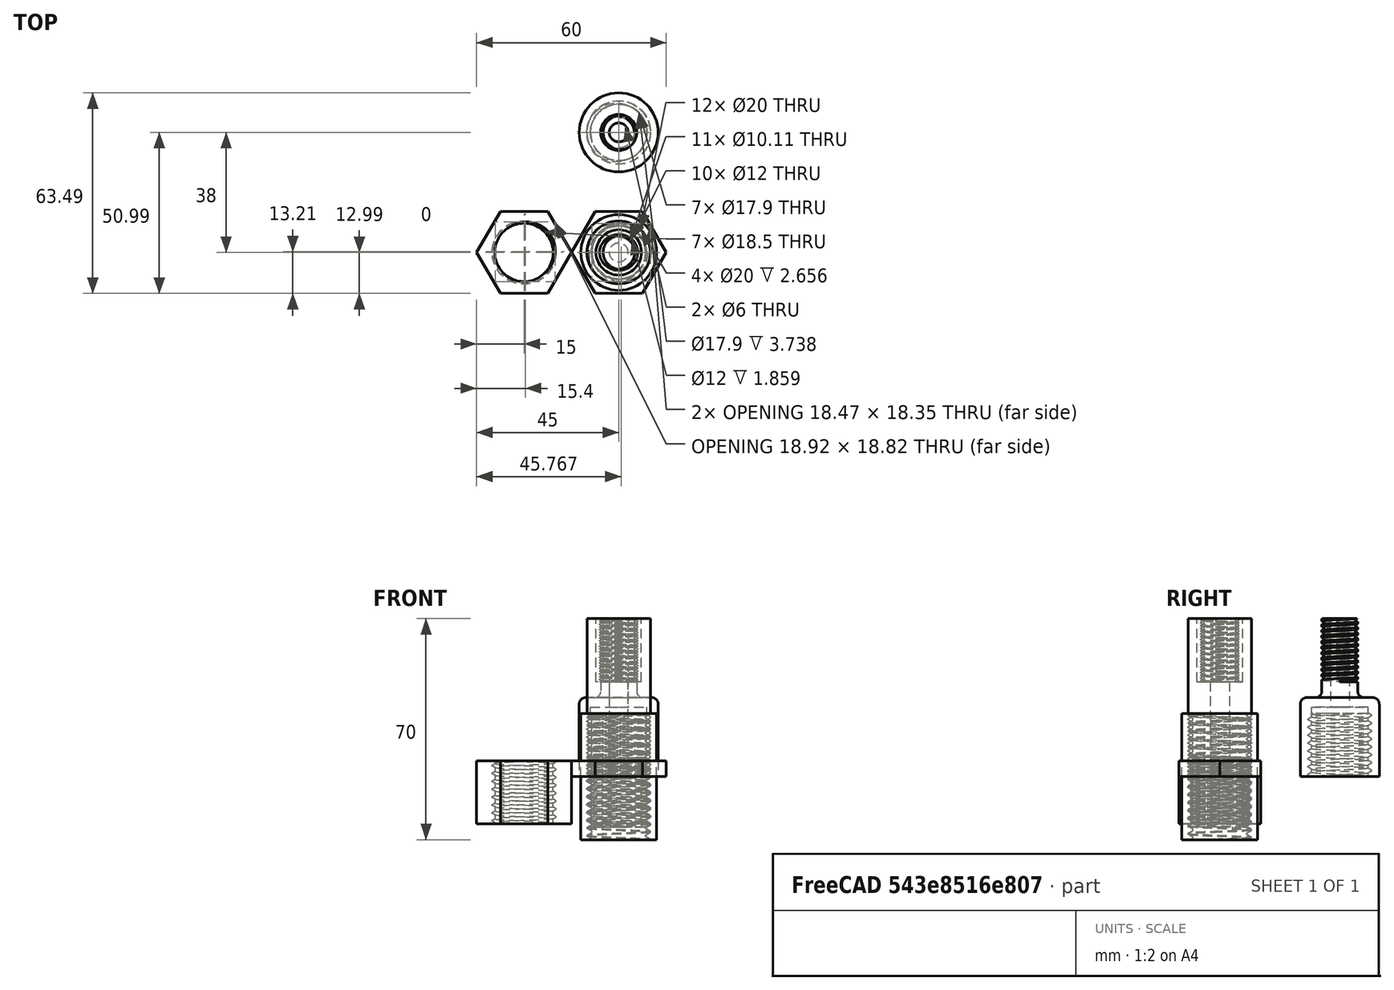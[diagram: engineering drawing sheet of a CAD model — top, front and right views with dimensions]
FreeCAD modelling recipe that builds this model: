
FCSTD DOCUMENT  (FreeCAD 1.0R39109 (Git))
Label: Fasteners_001
License: All rights reserved
LicenseURL: http://en.wikipedia.org/wiki/All_rights_reserved
objects: Part::FeaturePython×6, PartDesign::Boolean×6, Sketcher::SketchObject×5, PartDesign::Pad×4, PartDesign::Body×4, PartDesign::Revolution×1, PartDesign::Fillet×1, App::VarSet×1
note: 50 computed .brp shape members not serialized (recipe doc carries the construction recipe); baked Part::Feature solids carry a one-line shape summary decoded from their .brp

FEATURE [Sketcher::SketchObject] Sketch
  ArcFitTolerance = 1e-06
  AttachmentSupport = -> [XY_Plane]
  FullyConstrained = true
  MakeInternals = false
  MapMode = 5
  sketch-geometry (2):
    g0: Circle CenterX=0 CenterY=0 CenterZ=0 NormalX=0 NormalY=0 NormalZ=1 AngleXU=0 Radius=10
    g1: Circle CenterX=0 CenterY=0 CenterZ=0 NormalX=0 NormalY=0 NormalZ=1 AngleXU=0 Radius=3
  constraints (4):
    c: Diameter(g0) = 20
    c: Coincident(g0,g-1)
    c: Diameter(g1) = 6
    c: Coincident(g1,g0)
FEATURE [PartDesign::Pad] Pad
  Direction = (0,0,1)
  Length = 50
  Length2 = 10
  Profile = -> Sketch
  ReferenceAxis = -> Sketch [N_Axis]
  Refine = true
  Suppressed = false
  Type = 0
FEATURE [Part::FeaturePython] ScrewDie  label="20x20-ScrewDie"  # Fasteners workbench fastener (typed FeaturePython)
  Placement = pos=(0,0,20) rot=(0,0,1;0rad)
  diameter = 29
  diameterCustom = 20
  invert = true
  leftHanded = false
  length = 20
  matchOuter = false
  offset = 10
  pitchCustom = 2.5
  thread = true
  type = 0
FEATURE [PartDesign::Boolean] Boolean
  BaseFeature = -> Pad
  Group = -> [ScrewDie]
  Refine = true
  Suppressed = false
  Type = 1
  UsePlacement = true
FEATURE [Part::FeaturePython] ScrewTap  label="M12x20-ScrewTap"  # Fasteners workbench fastener (typed FeaturePython)
  Placement = pos=(0,0,50) rot=(0,0,1;0rad)
  diameter = 11
  diameterCustom = 6
  invert = false
  leftHanded = false
  length = 20
  matchOuter = false
  offset = 10
  pitchCustom = 1
  thread = true
  type = 2
FEATURE [Sketcher::SketchObject] Sketch001
  ArcFitTolerance = 1e-06
  AttachmentSupport = -> [XZ_Plane001]
  FullyConstrained = false
  MakeInternals = false
  MapMode = 5
  Placement = pos=(0,0,0) rot=(1,0,0;1.5708rad)
  expr: Constraints[13] = 17.5 mm / 2 + VarSet.Base_ScrewTapOffset
  expr: Constraints[14] = 12 mm / 2 - VarSet.Base_ScrewDieOffset
  expr: Constraints[5] = 25 / 2
  sketch-geometry (8):
    g0: LineSegment StartX=-5.7 StartY=50 StartZ=0 EndX=-5.7 EndY=25 EndZ=0
    g1: LineSegment StartX=-5.7 StartY=25 StartZ=0 EndX=-12.5 EndY=25 EndZ=0
    g2: LineSegment StartX=-12.5 StartY=25 StartZ=0 EndX=-12.5 EndY=0 EndZ=0
    g3: LineSegment StartX=-12.5 StartY=0 StartZ=0 EndX=-8.95 EndY=0 EndZ=0
    g4: LineSegment StartX=-8.95 StartY=0 StartZ=0 EndX=-8.95 EndY=22 EndZ=0
    g5: LineSegment StartX=-5.7 StartY=50 StartZ=0 EndX=-3 EndY=50 EndZ=0
    g6: LineSegment StartX=-3 StartY=50 StartZ=0 EndX=-3 EndY=22 EndZ=0
    g7: LineSegment StartX=-3 StartY=22 StartZ=0 EndX=-8.95 EndY=22 EndZ=0
  constraints (23):
    c: Vertical(g0)
    c: Coincident(g0,g1)
    c: Horizontal(g1)
    c: Coincident(g1,g2)
    c: Vertical(g2)
    c: DistanceX(g1,g-1) = 12.5
    c: DistanceY(g2,g1) = 25
    c: Coincident(g2,g3)
    c: PointOnObject(g3,g-1)
    c: Horizontal(g3)
    c: Coincident(g3,g4)
    c: Vertical(g4)
    c: DistanceY(g3,g4) = 22
    c: DistanceX(g3,g-1) = 8.95
    c: DistanceX(g0,g-1) = 5.7
    c: Coincident(g0,g5)
    c: Horizontal(g5)
    c: Coincident(g5,g6)
    c: Vertical(g6)
    c: Coincident(g6,g7)
    c: Coincident(g7,g4)
    c: Horizontal(g7)
    c: DistanceX(g5,g-1) = 3
FEATURE [PartDesign::Revolution] Revolution
  Angle = 360
  Angle2 = 60
  Axis = (0,2e-16,1)
  Base = (0,0,0)
  Placement = pos=(0,0,0) rot=(1,0,0;1.5708rad)
  Profile = -> Sketch001
  ReferenceAxis = -> Sketch001 [V_Axis]
  Refine = true
  Suppressed = false
  Type = 0
FEATURE [Part::FeaturePython] ScrewDie001  label="M12x20-ScrewDie"  # Fasteners workbench fastener (typed FeaturePython)
  Placement = pos=(0,0,50) rot=(0,0,1;0rad)
  diameter = 11
  diameterCustom = 6
  invert = false
  leftHanded = false
  length = 20
  matchOuter = false
  offset = 0
  pitchCustom = 1
  thread = true
  type = 0
  expr: .Placement.Base.z = 25 + 25
FEATURE [Part::FeaturePython] ScrewTap001  label="M20x20-ScrewTap"  # Fasteners workbench fastener (typed FeaturePython)
  Placement = pos=(0,0,20) rot=(0,0,1;0rad)
  diameter = 15
  diameterCustom = 6
  invert = false
  leftHanded = false
  length = 20
  matchOuter = false
  offset = 0
  pitchCustom = 1
  thread = true
  type = 2
FEATURE [PartDesign::Boolean] Boolean002
  BaseFeature = -> Revolution
  Group = -> [ScrewDie001]
  Refine = true
  Suppressed = false
  Type = 1
  UsePlacement = true
FEATURE [PartDesign::Boolean] Boolean003
  BaseFeature = -> Boolean002
  Group = -> [ScrewTap001]
  Refine = true
  Suppressed = false
  Type = 1
  UsePlacement = true
FEATURE [PartDesign::Boolean] Boolean004
  BaseFeature = -> Boolean
  Group = -> [ScrewTap]
  Refine = true
  Suppressed = false
  Type = 1
  UsePlacement = true
FEATURE [PartDesign::Body] Body
  AllowCompound = true
  Group = -> [Sketch,Pad,Boolean,Boolean004]
  Origin = -> Origin
  Tip = -> Boolean004
FEATURE [PartDesign::Fillet] Fillet
  Base = -> Boolean003 [Edge192,Edge212]
  BaseFeature = -> Boolean003
  Radius = 2
  Refine = true
  SupportTransform = false
  Suppressed = false
  UseAllEdges = false
FEATURE [PartDesign::Body] Body001
  AllowCompound = true
  Group = -> [Sketch001,Revolution,Boolean002,Boolean003,Fillet]
  Origin = -> Origin001
  Placement = pos=(0,38,0) rot=(0,0,1;0rad)
  Tip = -> Fillet
FEATURE [Sketcher::SketchObject] Sketch002
  ArcFitTolerance = 1e-06
  AttachmentSupport = -> [XY_Plane002]
  FullyConstrained = true
  MakeInternals = false
  MapMode = 5
  expr: Constraints[0] = 20 mm - VarSet.Base_ScrewDieOffset
  sketch-geometry (1):
    g0: Circle CenterX=0 CenterY=0 CenterZ=0 NormalX=0 NormalY=0 NormalZ=1 AngleXU=0 Radius=9.85
  constraints (2):
    c: Diameter(g0) = 19.7
    c: Coincident(g0,g-1)
FEATURE [PartDesign::Pad] Pad001
  Direction = (0,0,1)
  Length = 15
  Length2 = 10
  Profile = -> Sketch002
  ReferenceAxis = -> Sketch002 [N_Axis]
  Refine = true
  Reversed = true
  Suppressed = false
  Type = 0
FEATURE [Sketcher::SketchObject] Sketch003
  ArcFitTolerance = 1e-06
  AttachmentSupport = -> [XY_Plane002]
  FullyConstrained = true
  MakeInternals = false
  MapMode = 5
  sketch-geometry (7):
    g0: LineSegment StartX=15 StartY=0 StartZ=0 EndX=7.5 EndY=12.9904 EndZ=0
    g1: LineSegment StartX=7.5 StartY=12.9904 StartZ=0 EndX=-7.5 EndY=12.9904 EndZ=0
    g2: LineSegment StartX=-7.5 StartY=12.9904 StartZ=0 EndX=-15 EndY=1.8e-15 EndZ=0
    g3: LineSegment StartX=-15 StartY=1.8e-15 StartZ=0 EndX=-7.5 EndY=-12.9904 EndZ=0
    g4: LineSegment StartX=-7.5 StartY=-12.9904 StartZ=0 EndX=7.5 EndY=-12.9904 EndZ=0
    g5: LineSegment StartX=7.5 StartY=-12.9904 StartZ=0 EndX=15 EndY=0 EndZ=0
    g6: Circle [constr] CenterX=0 CenterY=0 CenterZ=0 NormalX=0 NormalY=0 NormalZ=1 AngleXU=0 Radius=15
  constraints (16):
    c: Coincident(g0,g1)
    c: Coincident(g1,g2)
    c: Coincident(g2,g3)
    c: Coincident(g3,g4)
    c: Coincident(g4,g5)
    c: Coincident(g5,g0)
    c: Equal(g0, g1-g5) x5
    c: PointOnObject(g0,g6)
    c: PointOnObject(g1,g6)
    c: PointOnObject(g2,g6)
    c: PointOnObject(g3,g6)
    c: PointOnObject(g4,g6)
    c: PointOnObject(g5,g6)
    c: Radius(g6) = 15
    c: Coincident(g6,g-1)
    c: PointOnObject(g5,g-1)
FEATURE [PartDesign::Pad] Pad002
  BaseFeature = -> Pad001
  Direction = (0,0,1)
  Length = 5
  Length2 = 10
  Profile = -> Sketch003
  ReferenceAxis = -> Sketch003 [N_Axis]
  Refine = true
  Suppressed = false
  Type = 0
FEATURE [Part::FeaturePython] ScrewDie002  label="M20x20-ScrewDie"  # Fasteners workbench fastener (typed FeaturePython)
  diameter = 15
  diameterCustom = 6
  invert = false
  leftHanded = false
  length = 20
  matchOuter = false
  offset = 0
  pitchCustom = 1
  thread = true
  type = 0
FEATURE [PartDesign::Boolean] Boolean005
  BaseFeature = -> Pad002
  Group = -> [ScrewDie002]
  Refine = true
  Suppressed = false
  Type = 1
  UsePlacement = true
FEATURE [PartDesign::Body] Body002
  AllowCompound = true
  Group = -> [Sketch002,Pad001,Sketch003,Pad002,Boolean005]
  Origin = -> Origin002
  Tip = -> Boolean005
FEATURE [App::VarSet] VarSet
  Base_ScrewDie = 0.1
  Base_ScrewDieOffset = 0.3
  Base_ScrewTapOffset = 0.2
FEATURE [Sketcher::SketchObject] Sketch004
  ArcFitTolerance = 1e-06
  AttachmentSupport = -> [XY_Plane003]
  FullyConstrained = true
  MakeInternals = false
  MapMode = 5
  expr: Constraints[21] = 18.5
  sketch-geometry (8):
    g0: LineSegment StartX=15 StartY=0 StartZ=0 EndX=7.5 EndY=12.9904 EndZ=0
    g1: LineSegment StartX=7.5 StartY=12.9904 StartZ=0 EndX=-7.5 EndY=12.9904 EndZ=0
    g2: LineSegment StartX=-7.5 StartY=12.9904 StartZ=0 EndX=-15 EndY=1.8e-15 EndZ=0
    g3: LineSegment StartX=-15 StartY=1.8e-15 StartZ=0 EndX=-7.5 EndY=-12.9904 EndZ=0
    g4: LineSegment StartX=-7.5 StartY=-12.9904 StartZ=0 EndX=7.5 EndY=-12.9904 EndZ=0
    g5: LineSegment StartX=7.5 StartY=-12.9904 StartZ=0 EndX=15 EndY=0 EndZ=0
    g6: Circle [constr] CenterX=0 CenterY=0 CenterZ=0 NormalX=0 NormalY=0 NormalZ=1 AngleXU=0 Radius=15
    g7: Circle CenterX=0 CenterY=0 CenterZ=0 NormalX=0 NormalY=0 NormalZ=1 AngleXU=0 Radius=9.25
  constraints (18):
    c: Coincident(g0,g1)
    c: Coincident(g1,g2)
    c: Coincident(g2,g3)
    c: Coincident(g3,g4)
    c: Coincident(g4,g5)
    c: Coincident(g5,g0)
    c: Equal(g0, g1-g5) x5
    c: PointOnObject(g0,g6)
    c: PointOnObject(g1,g6)
    c: PointOnObject(g2,g6)
    c: PointOnObject(g3,g6)
    c: PointOnObject(g4,g6)
    c: PointOnObject(g5,g6)
    c: Radius(g6) = 15
    c: Coincident(g6,g-1)
    c: PointOnObject(g5,g-1)
    c: Coincident(g7,g6)
    c: Diameter(g7) = 18.5
FEATURE [PartDesign::Pad] Pad003
  Direction = (0,0,1)
  Length = 15
  Length2 = 5
  Profile = -> Sketch004
  ReferenceAxis = -> Sketch004 [N_Axis]
  Refine = true
  Reversed = true
  Suppressed = false
  Type = 4
FEATURE [Part::FeaturePython] ScrewTap002  label="M20x22-ScrewTap"  # Fasteners workbench fastener (typed FeaturePython)
  Placement = pos=(0,0,6) rot=(0,0,1;0rad)
  diameter = 15
  diameterCustom = 6
  invert = false
  leftHanded = false
  length = 22
  matchOuter = false
  offset = 0
  pitchCustom = 1
  thread = true
  type = 2
FEATURE [PartDesign::Boolean] Boolean006
  BaseFeature = -> Pad003
  Group = -> [ScrewTap002]
  Refine = true
  Suppressed = false
  Type = 1
  UsePlacement = true
FEATURE [PartDesign::Body] Body003
  AllowCompound = true
  Group = -> [Sketch004,Pad003,Boolean006]
  Origin = -> Origin003
  Placement = pos=(-30,0,0) rot=(0,0,1;0rad)
  Tip = -> Boolean006
